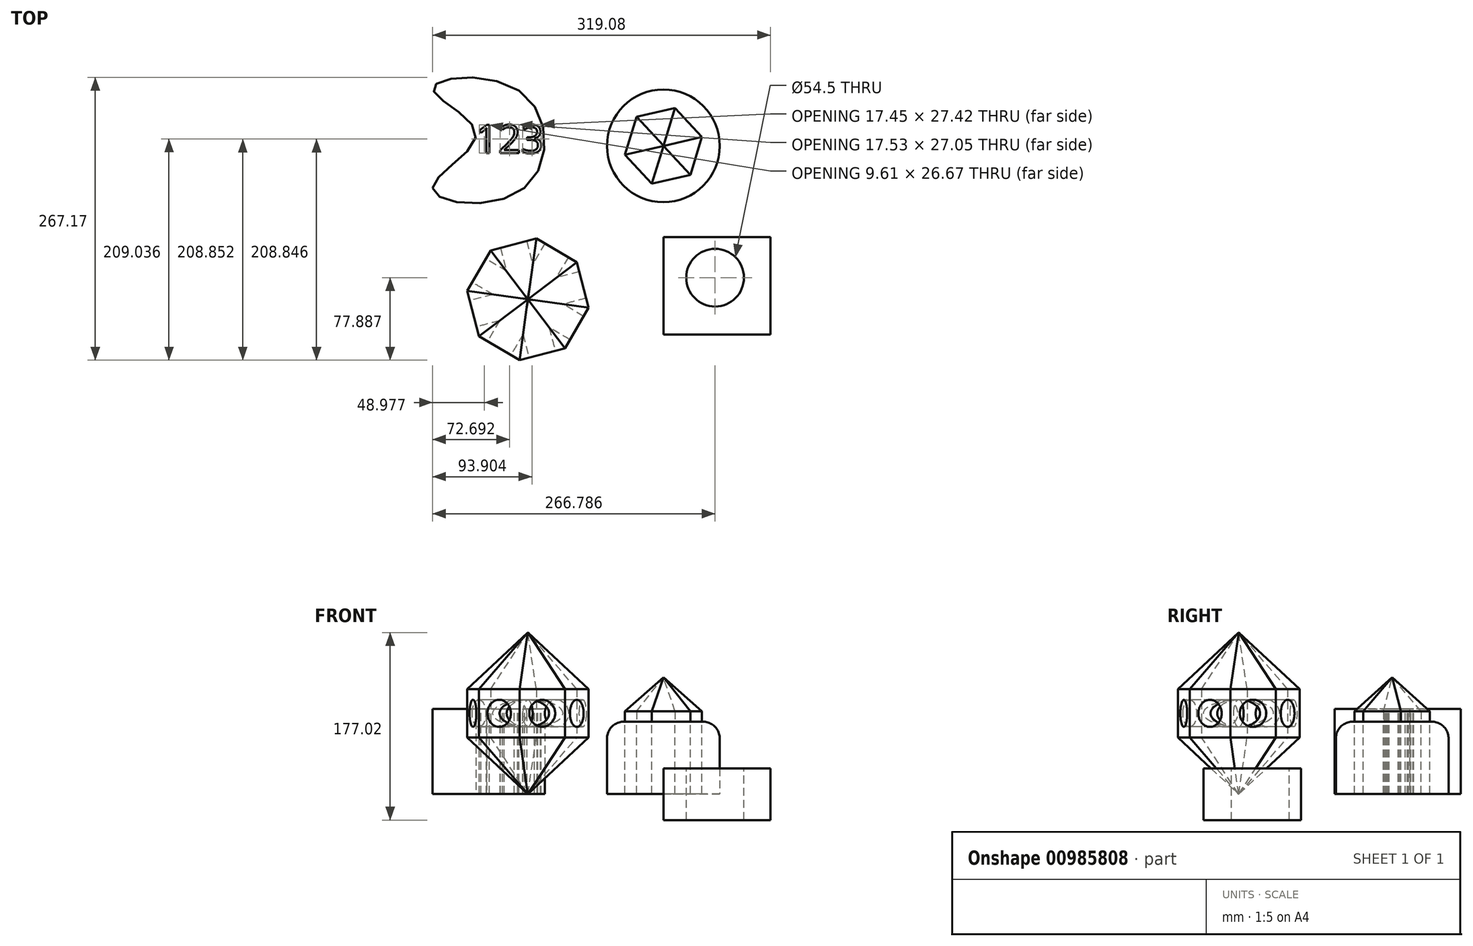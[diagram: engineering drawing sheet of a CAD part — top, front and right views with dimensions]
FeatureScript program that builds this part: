
annotation { "Feature Type Name" : "Feature", "Feature Type Description" : "" }
export const myFeature = defineFeature(function(context is Context, id is Id, definition is map)
    precondition{}
    {
        {
            var Q0;
            Q0=qCreatedBy(makeId("Top.planeOp"),FACE);
            var sketch = newSketch(context, id + "F0", { "sketchPlane" : qUnion([Q0])});
            skCircle(sketch, "E0", {"center": v(0, 0) * mm, "radius": 53.24 * mm});
            skSolve(sketch);
        }
        {
            var Q0;
            Q0 = qSketchRegion(id + "F0", true);
            extrude(context, id + "F1", {"entities" : qUnion([Q0]), "depth" : 68.33 * mm, "offsetDistance" : 25.4 * mm});
        }
        {
            var Q0;
            Q0=makeQuery(id+"F1.opExtrude","CAP_EDGE",EDGE,{"disambiguationData":[OSD([sQuery(id+"F0.wireOp",EDGE,"E0")])],"isStart":false});
            fillet(context, id + "F2", {"entities" : qUnion([Q0]), "radius" : 15.94 * mm, "tangentPropagation" : true, "allowEdgeOverflow" : false});
        }
        {
            var Q0;
            Q0=qCreatedBy(makeId("Right.planeOp"),FACE);
            var sketch = newSketch(context, id + "F3", { "sketchPlane" : qUnion([Q0])});
            skLineSegment(sketch, "E1.bottom", {"start": v(-178.12, 24.3) * mm, "end": v(-86.08, 24.3) * mm});
            skLineSegment(sketch, "E1.top", {"start": v(-178.12, -24.62) * mm, "end": v(-86.08, -24.62) * mm});
            skLineSegment(sketch, "E1.left", {"start": v(-178.12, 24.3) * mm, "end": v(-178.12, -24.62) * mm});
            skLineSegment(sketch, "E1.right", {"start": v(-86.08, 24.3) * mm, "end": v(-86.08, -24.62) * mm});
            skSolve(sketch);
        }
        {
            var Q0;
            Q0=makeQuery(id+"F3.imprint","IMPRINT",FACE,{"disambiguationData":[TD([[makeQuery(id+"F3.imprint","IMPRINT",EDGE,{"derivedFrom":sQuery(id+"F3.wireOp",EDGE,"E1.bottom")}),-1.0]])]});
            extrude(context, id + "F4", {"entities" : qUnion([Q0]), "depth" : 101.1 * mm, "offsetDistance" : 25.4 * mm});
        }
        {
            var Q0;
            Q0=makeQuery(id+"F4.opExtrude","SWEPT_FACE",FACE,{"disambiguationData":[OSD([sQuery(id+"F3.wireOp",EDGE,"E1.bottom")])]});
            var sketch = newSketch(context, id + "F5", { "sketchPlane" : qUnion([Q0])});
            skCircle(sketch, "E2", {"center": v(48.8, -124.52) * mm, "radius": 27.25 * mm});
            skSolve(sketch);
        }
        {
            var Q0;
            Q0=makeQuery(id+"F5.imprint","IMPRINT",FACE,{"disambiguationData":[TD([[makeQuery(id+"F5.imprint","IMPRINT",EDGE,{"derivedFrom":sQuery(id+"F5.wireOp",EDGE,"E2")}),1.0]])]});
            var Q1;
            Q1=sQuery(id+"F5.wireOp",EDGE,"E2");
            extrude(context, id + "F6", {"entities" : qUnion([Q0]), "operationType" : NewBodyOperationType.REMOVE, "surfaceEntities" : qUnion([Q1]), "oppositeDirection" : true, "depth" : 168.4 * mm, "offsetDistance" : 25.4 * mm});
        }
        {
            var Q0;
            Q0=makeQuery(id+"F1.opExtrude","CAP_FACE",FACE,{"disambiguationData":[OSD([sQuery(id+"F0.wireOp",EDGE,"E0")])],"isStart":false});
            var sketch = newSketch(context, id + "F7", { "sketchPlane" : qUnion([Q0])});
            skCircle(sketch, "E3.cCircle", {"center": v(0, 0) * mm, "radius": 37.3 * mm, "construction": true});
            skLineSegment(sketch, "E3.0", {"start": v(-25.37, 27.34) * mm, "end": v(10.99, 35.64) * mm});
            skLineSegment(sketch, "E3.1", {"start": v(10.99, 35.64) * mm, "end": v(36.36, 8.3) * mm});
            skLineSegment(sketch, "E3.2", {"start": v(36.36, 8.3) * mm, "end": v(25.37, -27.34) * mm});
            skLineSegment(sketch, "E3.3", {"start": v(25.37, -27.34) * mm, "end": v(-10.99, -35.64) * mm});
            skLineSegment(sketch, "E3.4", {"start": v(-10.99, -35.64) * mm, "end": v(-36.36, -8.3) * mm});
            skLineSegment(sketch, "E3.5", {"start": v(-36.36, -8.3) * mm, "end": v(-25.37, 27.34) * mm});
            skSolve(sketch);
        }
        {
            var Q0;
            Q0=makeQuery(id+"F7.imprint","IMPRINT",FACE,{"disambiguationData":[TD([[makeQuery(id+"F7.imprint","IMPRINT",EDGE,{"derivedFrom":sQuery(id+"F7.wireOp",EDGE,"E3.0")}),-1.0]])]});
            extrude(context, id + "F8", {"entities" : qUnion([Q0]), "operationType" : NewBodyOperationType.REMOVE, "oppositeDirection" : true, "depth" : 102.87 * mm, "offsetDistance" : 25.4 * mm});
        }
        {
            var Q0;
            Q0 = qSketchRegion(id + "F7", true);
            extrude(context, id + "F9", {"entities" : qUnion([Q0]), "depth" : 41.9 * mm, "offsetDistance" : 25.4 * mm});
        }
        {
            var Q0;
            Q0=qCreatedBy(makeId("Top.planeOp"),FACE);
            var sketch = newSketch(context, id + "F10", { "sketchPlane" : qUnion([Q0])});
            skFitSpline(sketch, "E4", {"points": [v(-218, -39.89) * mm, v(-134.22, -42.14) * mm, v(-134.67, 51.1) * mm, v(-217.54, 53.8) * mm, v(-177, 11) * mm, v(-218, -39.89) * mm]});
            skSolve(sketch);
        }
        {
            var Q0;
            Q0=makeQuery(id+"F10.imprint","IMPRINT",FACE,{"disambiguationData":[TD([[makeQuery(id+"F10.imprint","IMPRINT",EDGE,{"derivedFrom":sQuery(id+"F10.wireOp",EDGE,"E4")}),1.0]])]});
            extrude(context, id + "F11", {"entities" : qUnion([Q0]), "depth" : 80.26 * mm, "offsetDistance" : 25.4 * mm});
        }
        {
            var Q0;
            Q0=makeQuery(id+"F11.opExtrude","CAP_FACE",FACE,{"disambiguationData":[OSD([sQuery(id+"F10.wireOp",EDGE,"E4")])],"isStart":false});
            var sketch = newSketch(context, id + "F12", { "sketchPlane" : qUnion([Q0])});
            skText(sketch, "E5", { "text": "123\n", "fontName": "OpenSans-Regular.ttf"});
            const initialGuessF12  = {"E5": [-0.17725, -0.0069, 1, 0, 0.0269]};
            skSetInitialGuess(sketch, initialGuessF12);
            skSolve(sketch);
        }
        {
            var Q0;
            Q0 = qSketchRegion(id + "F12", true);
            extrude(context, id + "F13", {"entities" : qUnion([Q0]), "operationType" : NewBodyOperationType.REMOVE, "oppositeDirection" : true, "depth" : 142.75 * mm, "offsetDistance" : 25.4 * mm});
        }
        {
            var Q0;
            Q0=makeQuery(id+"F9.opExtrude","CAP_FACE",FACE,{"disambiguationData":[OSD([sQuery(id+"F7.wireOp",EDGE,"E3.0"),sQuery(id+"F7.wireOp",EDGE,"E3.1"),sQuery(id+"F7.wireOp",EDGE,"E3.2"),sQuery(id+"F7.wireOp",EDGE,"E3.3"),sQuery(id+"F7.wireOp",EDGE,"E3.4"),sQuery(id+"F7.wireOp",EDGE,"E3.5")])],"isStart":false});
            var Q1;
            Q1=makeQuery(id+"F9.opExtrude","CAP_EDGE",EDGE,{"disambiguationData":[OSD([sQuery(id+"F7.wireOp",EDGE,"E3.3")])],"isStart":false});
            chamfer(context, id + "F14", {"entities" : qUnion([Q0, Q1]), "width" : 32.26 * mm, "tangentPropagation" : true});
        }
        {
            var Q0;
            Q0=qCreatedBy(makeId("Top.planeOp"),FACE);
            var sketch = newSketch(context, id + "F15", { "sketchPlane" : qUnion([Q0])});
            skCircle(sketch, "E6.cCircle", {"center": v(-128, -144.97) * mm, "radius": 53.57 * mm, "construction": true});
            skLineSegment(sketch, "E6.0", {"start": v(-70.57, -152.91) * mm, "end": v(-93, -191.2) * mm});
            skLineSegment(sketch, "E6.1", {"start": v(-93, -191.2) * mm, "end": v(-135.94, -202.4) * mm});
            skLineSegment(sketch, "E6.2", {"start": v(-135.94, -202.4) * mm, "end": v(-174.23, -179.97) * mm});
            skLineSegment(sketch, "E6.3", {"start": v(-174.23, -179.97) * mm, "end": v(-185.44, -137.04) * mm});
            skLineSegment(sketch, "E6.4", {"start": v(-185.44, -137.04) * mm, "end": v(-163, -98.75) * mm});
            skLineSegment(sketch, "E6.5", {"start": v(-163, -98.75) * mm, "end": v(-120.07, -87.54) * mm});
            skLineSegment(sketch, "E6.6", {"start": v(-120.07, -87.54) * mm, "end": v(-81.78, -109.97) * mm});
            skLineSegment(sketch, "E6.7", {"start": v(-81.78, -109.97) * mm, "end": v(-70.57, -152.91) * mm});
            skPoint(sketch, "E6.0.midPoint", {"position": v(-81.78, -172.05) * mm});
            skSolve(sketch);
        }
        {
            var Q0;
            Q0=makeQuery(id+"F15.imprint","IMPRINT",FACE,{"disambiguationData":[TD([[makeQuery(id+"F15.imprint","IMPRINT",EDGE,{"derivedFrom":sQuery(id+"F15.wireOp",EDGE,"E6.0")}),-1.0]])]});
            extrude(context, id + "F16", {"entities" : qUnion([Q0]), "depth" : 152.4 * mm, "offsetDistance" : 25.4 * mm});
        }
        {
            var Q0;
            Q0=makeQuery(id+"F16.opExtrude","CAP_FACE",FACE,{"disambiguationData":[OSD([sQuery(id+"F15.wireOp",EDGE,"E6.0"),sQuery(id+"F15.wireOp",EDGE,"E6.1"),sQuery(id+"F15.wireOp",EDGE,"E6.2"),sQuery(id+"F15.wireOp",EDGE,"E6.3"),sQuery(id+"F15.wireOp",EDGE,"E6.4"),sQuery(id+"F15.wireOp",EDGE,"E6.5"),sQuery(id+"F15.wireOp",EDGE,"E6.6"),sQuery(id+"F15.wireOp",EDGE,"E6.7")])],"isStart":false});
            chamfer(context, id + "F17", {"entities" : qUnion([Q0]), "width" : 53.34 * mm, "tangentPropagation" : true});
        }
        {
            var Q0;
            Q0=makeQuery(id+"F16.opExtrude","CAP_FACE",FACE,{"disambiguationData":[OSD([sQuery(id+"F15.wireOp",EDGE,"E6.0"),sQuery(id+"F15.wireOp",EDGE,"E6.1"),sQuery(id+"F15.wireOp",EDGE,"E6.2"),sQuery(id+"F15.wireOp",EDGE,"E6.3"),sQuery(id+"F15.wireOp",EDGE,"E6.4"),sQuery(id+"F15.wireOp",EDGE,"E6.5"),sQuery(id+"F15.wireOp",EDGE,"E6.6"),sQuery(id+"F15.wireOp",EDGE,"E6.7")])],"isStart":true});
            chamfer(context, id + "F18", {"entities" : qUnion([Q0]), "width" : 53.34 * mm, "tangentPropagation" : true});
        }
        {
            var Q0;
            Q0=makeQuery(id+"F16.opExtrude","SWEPT_FACE",FACE,{"disambiguationData":[OSD([sQuery(id+"F15.wireOp",EDGE,"E6.1")])]});
            var sketch = newSketch(context, id + "F19", { "sketchPlane" : qUnion([Q0])});
            skPoint(sketch, "E7.centerSnap0", {"position": v(-182.66, 76.2) * mm});
            skPoint(sketch, "E7.centerSnap1", {"position": v(-160.47, 99.06) * mm});
            skCircle(sketch, "E8", {"center": v(-160.47, 76.2) * mm, "radius": 12.7 * mm});
            skSolve(sketch);
        }
        {
            var Q0;
            Q0=makeQuery(id+"F19.imprint","IMPRINT",FACE,{"disambiguationData":[TD([[makeQuery(id+"F19.imprint","IMPRINT",EDGE,{"derivedFrom":sQuery(id+"F19.wireOp",EDGE,"E8")}),1.0]])]});
            extrude(context, id + "F20", {"entities" : qUnion([Q0]), "operationType" : NewBodyOperationType.REMOVE, "oppositeDirection" : true, "depth" : 120.65 * mm, "offsetDistance" : 25.4 * mm});
        }
        {
            var Q0;
            Q0=makeQuery(id+"F16.opExtrude","SWEPT_FACE",FACE,{"disambiguationData":[OSD([sQuery(id+"F15.wireOp",EDGE,"E6.2")])]});
            var sketch = newSketch(context, id + "F21", { "sketchPlane" : qUnion([Q0])});
            skCircle(sketch, "E9", {"center": v(-37.15, 76.2) * mm, "radius": 12.83 * mm});
            skPoint(sketch, "E9.centerSnap0", {"position": v(-37.15, 99.06) * mm});
            skPoint(sketch, "E9.centerSnap1", {"position": v(-59.34, 76.2) * mm});
            skSolve(sketch);
        }
        {
            var Q0;
            Q0=makeQuery(id+"F21.imprint","IMPRINT",FACE,{"disambiguationData":[TD([[makeQuery(id+"F21.imprint","IMPRINT",EDGE,{"derivedFrom":sQuery(id+"F21.wireOp",EDGE,"E9")}),1.0]])]});
            extrude(context, id + "F22", {"entities" : qUnion([Q0]), "operationType" : NewBodyOperationType.REMOVE, "oppositeDirection" : true, "depth" : 125.73 * mm, "offsetDistance" : 25.4 * mm});
        }
        {
            var Q0;
            Q0=makeQuery(id+"F16.opExtrude","SWEPT_FACE",FACE,{"disambiguationData":[OSD([sQuery(id+"F15.wireOp",EDGE,"E6.3")])]});
            var sketch = newSketch(context, id + "F23", { "sketchPlane" : qUnion([Q0])});
            skCircle(sketch, "E10", {"center": v(107.94, 76.2) * mm, "radius": 12.86 * mm});
            skPoint(sketch, "E10.centerSnap0", {"position": v(107.94, 99.06) * mm});
            skPoint(sketch, "E10.centerSnap1", {"position": v(85.75, 76.2) * mm});
            skSolve(sketch);
        }
        {
            var Q0;
            Q0=makeQuery(id+"F23.imprint","IMPRINT",FACE,{"disambiguationData":[TD([[makeQuery(id+"F23.imprint","IMPRINT",EDGE,{"derivedFrom":sQuery(id+"F23.wireOp",EDGE,"E10")}),1.0]])]});
            extrude(context, id + "F24", {"entities" : qUnion([Q0]), "operationType" : NewBodyOperationType.REMOVE, "oppositeDirection" : true, "depth" : 129.03 * mm, "offsetDistance" : 25.4 * mm});
        }
        {
            var Q0;
            Q0=makeQuery(id+"F16.opExtrude","SWEPT_FACE",FACE,{"disambiguationData":[OSD([sQuery(id+"F15.wireOp",EDGE,"E6.4")])]});
            var sketch = newSketch(context, id + "F25", { "sketchPlane" : qUnion([Q0])});
            skCircle(sketch, "E11", {"center": v(189.8, 76.2) * mm, "radius": 12.79 * mm});
            skPoint(sketch, "E11.centerSnap0", {"position": v(189.8, 99.06) * mm});
            skPoint(sketch, "E11.centerSnap1", {"position": v(211.98, 76.2) * mm});
            skSolve(sketch);
        }
        {
            var Q0;
            Q0=makeQuery(id+"F25.imprint","IMPRINT",FACE,{"disambiguationData":[TD([[makeQuery(id+"F25.imprint","IMPRINT",EDGE,{"derivedFrom":sQuery(id+"F25.wireOp",EDGE,"E11")}),1.0]])]});
            extrude(context, id + "F26", {"entities" : qUnion([Q0]), "operationType" : NewBodyOperationType.REMOVE, "oppositeDirection" : true, "depth" : 111.76 * mm, "offsetDistance" : 25.4 * mm});
        }
    });
